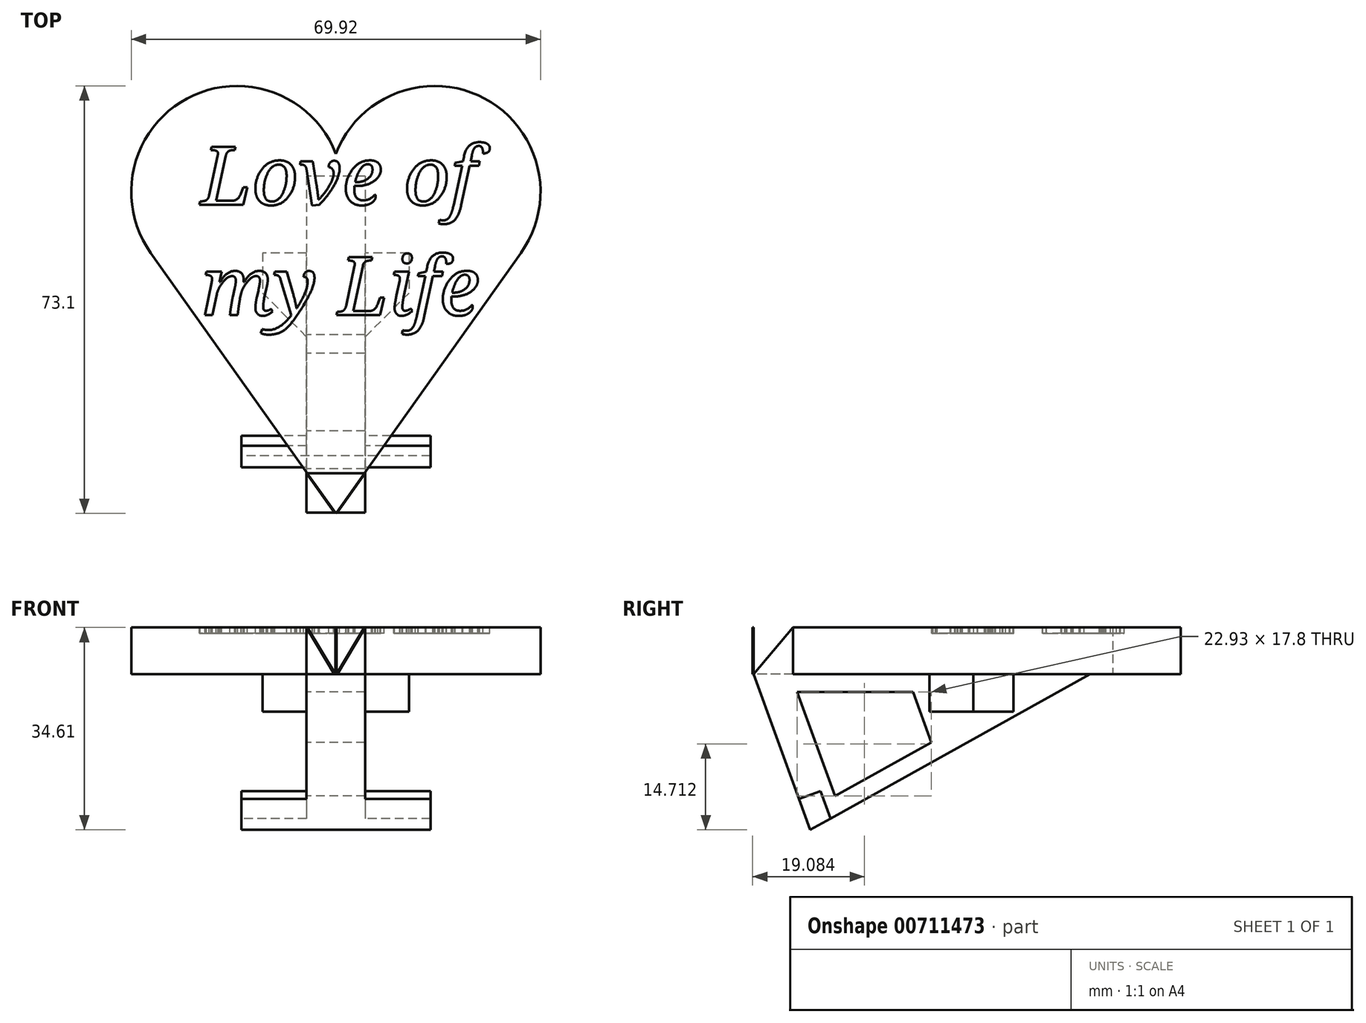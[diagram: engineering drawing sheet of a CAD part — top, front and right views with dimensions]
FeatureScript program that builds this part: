
annotation { "Feature Type Name" : "Feature", "Feature Type Description" : "" }
export const myFeature = defineFeature(function(context is Context, id is Id, definition is map)
    precondition{}
    {
        {
            var Q0;
            Q0=qCreatedBy(makeId("Top.planeOp"),FACE);
            var sketch = newSketch(context, id + "F0", { "sketchPlane" : qUnion([Q0])});
            skLineSegment(sketch, "E0", {"start": v(-31.62, 0) * mm, "end": v(0, -44.55) * mm});
            skLineSegment(sketch, "E1.MirrorCS", {"start": v(31.62, 0) * mm, "end": v(0, -44.55) * mm});
            skArc(sketch, "E2", {"start": v(-31.62, 0) * mm, "mid": v(-25.42, 26.4) * mm, "end": v(0, 16.97) * mm});
            skArc(sketch, "E3.MirrorCS", {"start": v(31.62, 0) * mm, "mid": v(25.42, 26.4) * mm, "end": v(0, 16.97) * mm});
            skSolve(sketch);
        }
        {
            var Q0;
            Q0=makeQuery(id+"F0.imprint","IMPRINT",FACE,{"disambiguationData":[TD([[makeQuery(id+"F0.imprint","IMPRINT",EDGE,{"derivedFrom":sQuery(id+"F0.wireOp",EDGE,"E0")}),1.0]])]});
            extrude(context, id + "F1", {"entities" : qUnion([Q0]), "depth" : 8 * mm, "offsetDistance" : 25 * mm});
        }
        {
            var Q0;
            Q0=makeQuery(id+"F1.opExtrude","CAP_FACE",FACE,{"disambiguationData":[OSD([sQuery(id+"F0.wireOp",EDGE,"E0"),sQuery(id+"F0.wireOp",EDGE,"E1.MirrorCS"),sQuery(id+"F0.wireOp",EDGE,"E2"),sQuery(id+"F0.wireOp",EDGE,"E3.MirrorCS")])],"isStart":false});
            var sketch = newSketch(context, id + "F2", { "sketchPlane" : qUnion([Q0])});
            skText(sketch, "E4", { "text": "Love of \nmy Life", "fontName": "NotoSerif-Italic.ttf"});
            const initialGuessF2  = {"E4": [-0.023, 0.00825, 1, 0, 0.01]};
            skSetInitialGuess(sketch, initialGuessF2);
            skSolve(sketch);
        }
        {
            var Q0;
            Q0 = qSketchRegion(id + "F2", true);
            extrude(context, id + "F3", {"entities" : qUnion([Q0]), "operationType" : NewBodyOperationType.REMOVE, "oppositeDirection" : true, "depth" : 1 * mm, "offsetDistance" : 25 * mm});
        }
        {
            var Q0;
            Q0=qCreatedBy(makeId("Right.planeOp"),FACE);
            var sketch = newSketch(context, id + "F4", { "sketchPlane" : qUnion([Q0])});
            skLineSegment(sketch, "E5", {"start": v(13.1, 0) * mm, "end": v(-34.72, -26.6) * mm});
            skLineSegment(sketch, "E6", {"start": v(-34.72, -26.6) * mm, "end": v(-44.4, 0) * mm});
            skLineSegment(sketch, "E7", {"start": v(13.1, 0) * mm, "end": v(-44.4, 0) * mm});
            skSolve(sketch);
        }
        {
            var Q0;
            Q0=makeQuery(id+"F4.imprint","IMPRINT",FACE,{"disambiguationData":[TD([[makeQuery(id+"F4.imprint","IMPRINT",EDGE,{"derivedFrom":sQuery(id+"F4.wireOp",EDGE,"E5")}),-1.0]])]});
            extrude(context, id + "F5", {"entities" : qUnion([Q0]), "endBound" : BoundingType.SYMMETRIC, "depth" : 10 * mm, "offsetDistance" : 25 * mm});
        }
        {
            var Q0;
            Q0=makeQuery(id+"F5.opExtrude","SWEPT_FACE",FACE,{"disambiguationData":[OSD([sQuery(id+"F4.wireOp",EDGE,"E7")])]});
            var sketch = newSketch(context, id + "F6", { "sketchPlane" : qUnion([Q0])});
            skLineSegment(sketch, "E8", {"start": v(-5, -37.66) * mm, "end": v(-0.25, -44.4) * mm});
            skLineSegment(sketch, "E9", {"start": v(-0.25, -44.4) * mm, "end": v(-5, -44.4) * mm});
            skLineSegment(sketch, "E10", {"start": v(-5, -44.4) * mm, "end": v(-5, -37.66) * mm});
            skLineSegment(sketch, "E11.MirrorCS", {"start": v(5, -37.66) * mm, "end": v(0.25, -44.4) * mm});
            skLineSegment(sketch, "E12.MirrorCS", {"start": v(0.25, -44.4) * mm, "end": v(5, -44.4) * mm});
            skLineSegment(sketch, "E13.MirrorCS", {"start": v(5, -44.4) * mm, "end": v(5, -37.66) * mm});
            skSolve(sketch);
        }
        {
            var Q0;
            Q0=makeQuery(id+"F6.imprint","IMPRINT",FACE,{"disambiguationData":[TD([[makeQuery(id+"F6.imprint","IMPRINT",EDGE,{"derivedFrom":sQuery(id+"F6.wireOp",EDGE,"E8")}),-1.0]])]});
            var Q1;
            Q1=makeQuery(id+"F6.imprint","IMPRINT",FACE,{"disambiguationData":[TD([[makeQuery(id+"F6.imprint","IMPRINT",EDGE,{"derivedFrom":sQuery(id+"F6.wireOp",EDGE,"E11.MirrorCS")}),1.0]])]});
            extrude(context, id + "F7", {"entities" : qUnion([Q0, Q1]), "operationType" : NewBodyOperationType.ADD, "depth" : 8 * mm, "offsetDistance" : 25 * mm});
        }
        {
            var Q0;
            Q0=makeQuery(id+"F5.opExtrude","SWEPT_FACE",FACE,{"disambiguationData":[OSD([sQuery(id+"F4.wireOp",EDGE,"E6")])]});
            var sketch = newSketch(context, id + "F8", { "sketchPlane" : qUnion([Q0])});
            skLineSegment(sketch, "E14.bottom", {"start": v(16.17, -13.13) * mm, "end": v(-16.17, -13.13) * mm});
            skLineSegment(sketch, "E14.top", {"start": v(16.17, -7.49) * mm, "end": v(-16.17, -7.49) * mm});
            skLineSegment(sketch, "E14.left", {"start": v(16.17, -13.13) * mm, "end": v(16.17, -7.49) * mm});
            skLineSegment(sketch, "E14.right", {"start": v(-16.17, -13.13) * mm, "end": v(-16.17, -7.49) * mm});
            skPoint(sketch, "E14.middle", {"position": v(0, -10.3) * mm});
            skPoint(sketch, "E14.cornerSnap0", {"position": v(0, -13.13) * mm});
            skSolve(sketch);
        }
        {
            var Q0;
            {var subQ3=sQuery(id+"F8.wireOp",EDGE,"E14.left");Q0=makeQuery(id+"F8.imprint","IMPRINT",FACE,{"disambiguationData":[TD([[makeQuery(id+"F8.imprint","IMPRINT",EDGE,{"derivedFrom":subQ3}),1.0]])]});}
            var Q1;
            {var subQ3=sQuery(id+"F8.wireOp",EDGE,"E14.right");Q1=makeQuery(id+"F8.imprint","IMPRINT",FACE,{"disambiguationData":[TD([[makeQuery(id+"F8.imprint","IMPRINT",EDGE,{"derivedFrom":subQ3}),-1.0]])]});}
            var Q2;
            {var subQ0=sQuery(id+"F8.wireOp",EDGE,"E14.bottom");var subQ1=sQuery(id+"F4.wireOp",EDGE,"E6");var subQ2=makeQuery(id+"F5.opExtrude","CAP_EDGE",EDGE,{"disambiguationData":[OSD([subQ1])],"isStart":true});var subQ3=makeQuery(id+"F8.imprint","INTERSECT",VERTEX,{"derivedFrom":[subQ2,subQ0]});Q2=makeQuery(id+"F8.imprint","IMPRINT",FACE,{"disambiguationData":[TD([[makeQuery(id+"F8.imprint","IMPRINT",EDGE,{"disambiguationData":[TD([[subQ3,1.0]])],"derivedFrom":subQ0}),-1.0]])]});}
            extrude(context, id + "F9", {"entities" : qUnion([Q0, Q1, Q2]), "operationType" : NewBodyOperationType.ADD, "oppositeDirection" : true, "depth" : 3.9 * mm, "offsetDistance" : 25 * mm});
        }
        {
            var Q0;
            Q0=makeQuery(id+"F7.boolean.opBoolean","MERGE",FACE,{"derivedFrom":[makeQuery(id+"F5.opExtrude","CAP_FACE",FACE,{"disambiguationData":[OSD([sQuery(id+"F4.wireOp",EDGE,"E5"),sQuery(id+"F4.wireOp",EDGE,"E6"),sQuery(id+"F4.wireOp",EDGE,"E7")])],"isStart":false}),makeQuery(id+"F7.opExtrude","SWEPT_FACE",FACE,{"disambiguationData":[OSD([sQuery(id+"F6.wireOp",EDGE,"E13.MirrorCS")])]})]});
            var sketch = newSketch(context, id + "F10", { "sketchPlane" : qUnion([Q0])});
            skLineSegment(sketch, "E15", {"start": v(-36.65, -21.3) * mm, "end": v(-33.6, -29.7) * mm});
            skLineSegment(sketch, "E16", {"start": v(-28.62, -23.21) * mm, "end": v(-34.72, -26.6) * mm});
            skLineSegment(sketch, "E17", {"start": v(-33.6, -29.7) * mm, "end": v(-28.62, -23.21) * mm});
            skSolve(sketch);
        }
        {
            var Q0;
            {var subQ0=sQuery(id+"F10.wireOp",EDGE,"E17");Q0=makeQuery(id+"F10.imprint","IMPRINT",FACE,{"disambiguationData":[TD([[makeQuery(id+"F10.imprint","IMPRINT",EDGE,{"derivedFrom":subQ0}),1.0]])]});}
            extrude(context, id + "F11", {"entities" : qUnion([Q0]), "operationType" : NewBodyOperationType.REMOVE, "endBound" : BoundingType.SYMMETRIC, "oppositeDirection" : true, "depth" : 50.6 * mm, "offsetDistance" : 25 * mm});
        }
        {
            var Q0;
            Q0=qCreatedBy(makeId("Right.planeOp"),FACE);
            var sketch = newSketch(context, id + "F12", { "sketchPlane" : qUnion([Q0])});
            skLineSegment(sketch, "E18.bottom", {"start": v(0, 0) * mm, "end": v(-6.87, 0) * mm});
            skLineSegment(sketch, "E18.top", {"start": v(0, -6.37) * mm, "end": v(-6.87, -6.37) * mm});
            skLineSegment(sketch, "E18.left", {"start": v(0, 0) * mm, "end": v(0, -6.37) * mm});
            skLineSegment(sketch, "E18.right", {"start": v(-6.87, 0) * mm, "end": v(-6.87, -6.37) * mm});
            skPoint(sketch, "E18.middle", {"position": v(-3.43, -3.18) * mm});
            skSolve(sketch);
        }
        {
            var Q0;
            Q0 = qSketchRegion(id + "F12", true);
            extrude(context, id + "F13", {"entities" : qUnion([Q0]), "operationType" : NewBodyOperationType.ADD, "endBound" : BoundingType.SYMMETRIC, "depth" : 25 * mm, "offsetDistance" : 25 * mm});
        }
        {
            var Q0;
            Q0=makeQuery(id+"F13.boolean.opBoolean","INTERSECT",EDGE,{"derivedFrom":[makeQuery(id+"F7.boolean.opBoolean","MERGE",FACE,{"derivedFrom":[makeQuery(id+"F5.opExtrude","CAP_FACE",FACE,{"disambiguationData":[OSD([sQuery(id+"F4.wireOp",EDGE,"E5"),sQuery(id+"F4.wireOp",EDGE,"E6"),sQuery(id+"F4.wireOp",EDGE,"E7")])],"isStart":true}),makeQuery(id+"F7.opExtrude","SWEPT_FACE",FACE,{"disambiguationData":[OSD([sQuery(id+"F6.wireOp",EDGE,"E10")])]})]}),makeQuery(id+"F13.opExtrude","SWEPT_FACE",FACE,{"disambiguationData":[OSD([sQuery(id+"F12.wireOp",EDGE,"E18.right")])]})]});
            var Q1;
            Q1=makeQuery(id+"F13.boolean.opBoolean","INTERSECT",EDGE,{"derivedFrom":[makeQuery(id+"F7.boolean.opBoolean","MERGE",FACE,{"derivedFrom":[makeQuery(id+"F5.opExtrude","CAP_FACE",FACE,{"disambiguationData":[OSD([sQuery(id+"F4.wireOp",EDGE,"E5"),sQuery(id+"F4.wireOp",EDGE,"E6"),sQuery(id+"F4.wireOp",EDGE,"E7")])],"isStart":false}),makeQuery(id+"F7.opExtrude","SWEPT_FACE",FACE,{"disambiguationData":[OSD([sQuery(id+"F6.wireOp",EDGE,"E13.MirrorCS")])]})]}),makeQuery(id+"F13.opExtrude","SWEPT_FACE",FACE,{"disambiguationData":[OSD([sQuery(id+"F12.wireOp",EDGE,"E18.right")])]})]});
            chamfer(context, id + "F14", {"entities" : qUnion([Q0, Q1]), "width" : 7.5 * mm, "tangentPropagation" : true});
        }
        {
            var Q0;
            Q0=makeQuery(id+"F7.boolean.opBoolean","MERGE",FACE,{"derivedFrom":[makeQuery(id+"F5.opExtrude","CAP_FACE",FACE,{"disambiguationData":[OSD([sQuery(id+"F4.wireOp",EDGE,"E5"),sQuery(id+"F4.wireOp",EDGE,"E6"),sQuery(id+"F4.wireOp",EDGE,"E7")])],"isStart":true}),makeQuery(id+"F7.opExtrude","SWEPT_FACE",FACE,{"disambiguationData":[OSD([sQuery(id+"F6.wireOp",EDGE,"E10")])]})]});
            var sketch = newSketch(context, id + "F15", { "sketchPlane" : qUnion([Q0])});
            skLineSegment(sketch, "E19", {"start": v(14, -11.64) * mm, "end": v(30.45, -20.8) * mm});
            skLineSegment(sketch, "E20", {"start": v(30.45, -20.8) * mm, "end": v(36.93, -3) * mm});
            skLineSegment(sketch, "E21", {"start": v(36.93, -3) * mm, "end": v(17.15, -3) * mm});
            skLineSegment(sketch, "E22", {"start": v(17.15, -3) * mm, "end": v(14, -11.64) * mm});
            skSolve(sketch);
        }
        {
            var Q0;
            Q0=makeQuery(id+"F15.imprint","IMPRINT",FACE,{"disambiguationData":[TD([[makeQuery(id+"F15.imprint","IMPRINT",EDGE,{"derivedFrom":sQuery(id+"F15.wireOp",EDGE,"E19")}),1.0]])]});
            extrude(context, id + "F16", {"entities" : qUnion([Q0]), "operationType" : NewBodyOperationType.REMOVE, "oppositeDirection" : true, "depth" : 25 * mm, "offsetDistance" : 25 * mm});
        }
        {
            var Q0;
            Q0=makeQuery(id+"F7.boolean.opBoolean","MERGE",FACE,{"derivedFrom":[makeQuery(id+"F5.opExtrude","CAP_FACE",FACE,{"disambiguationData":[OSD([sQuery(id+"F4.wireOp",EDGE,"E5"),sQuery(id+"F4.wireOp",EDGE,"E6"),sQuery(id+"F4.wireOp",EDGE,"E7")])],"isStart":true}),makeQuery(id+"F7.opExtrude","SWEPT_FACE",FACE,{"disambiguationData":[OSD([sQuery(id+"F6.wireOp",EDGE,"E10")])]})]});
            var sketch = newSketch(context, id + "F17", { "sketchPlane" : qUnion([Q0])});
            skLineSegment(sketch, "E23", {"start": v(37.66, 8) * mm, "end": v(44.4, 0) * mm});
            skLineSegment(sketch, "E24", {"start": v(44.4, 0) * mm, "end": v(44.4, 8) * mm});
            skLineSegment(sketch, "E25", {"start": v(44.4, 8) * mm, "end": v(37.66, 8) * mm});
            skSolve(sketch);
        }
        {
            var Q0;
            Q0=makeQuery(id+"F17.imprint","IMPRINT",FACE,{"disambiguationData":[TD([[makeQuery(id+"F17.imprint","IMPRINT",EDGE,{"derivedFrom":sQuery(id+"F17.wireOp",EDGE,"E23")}),1.0]])]});
            extrude(context, id + "F18", {"entities" : qUnion([Q0]), "operationType" : NewBodyOperationType.REMOVE, "oppositeDirection" : true, "depth" : 25 * mm, "offsetDistance" : 25 * mm});
        }
    });
